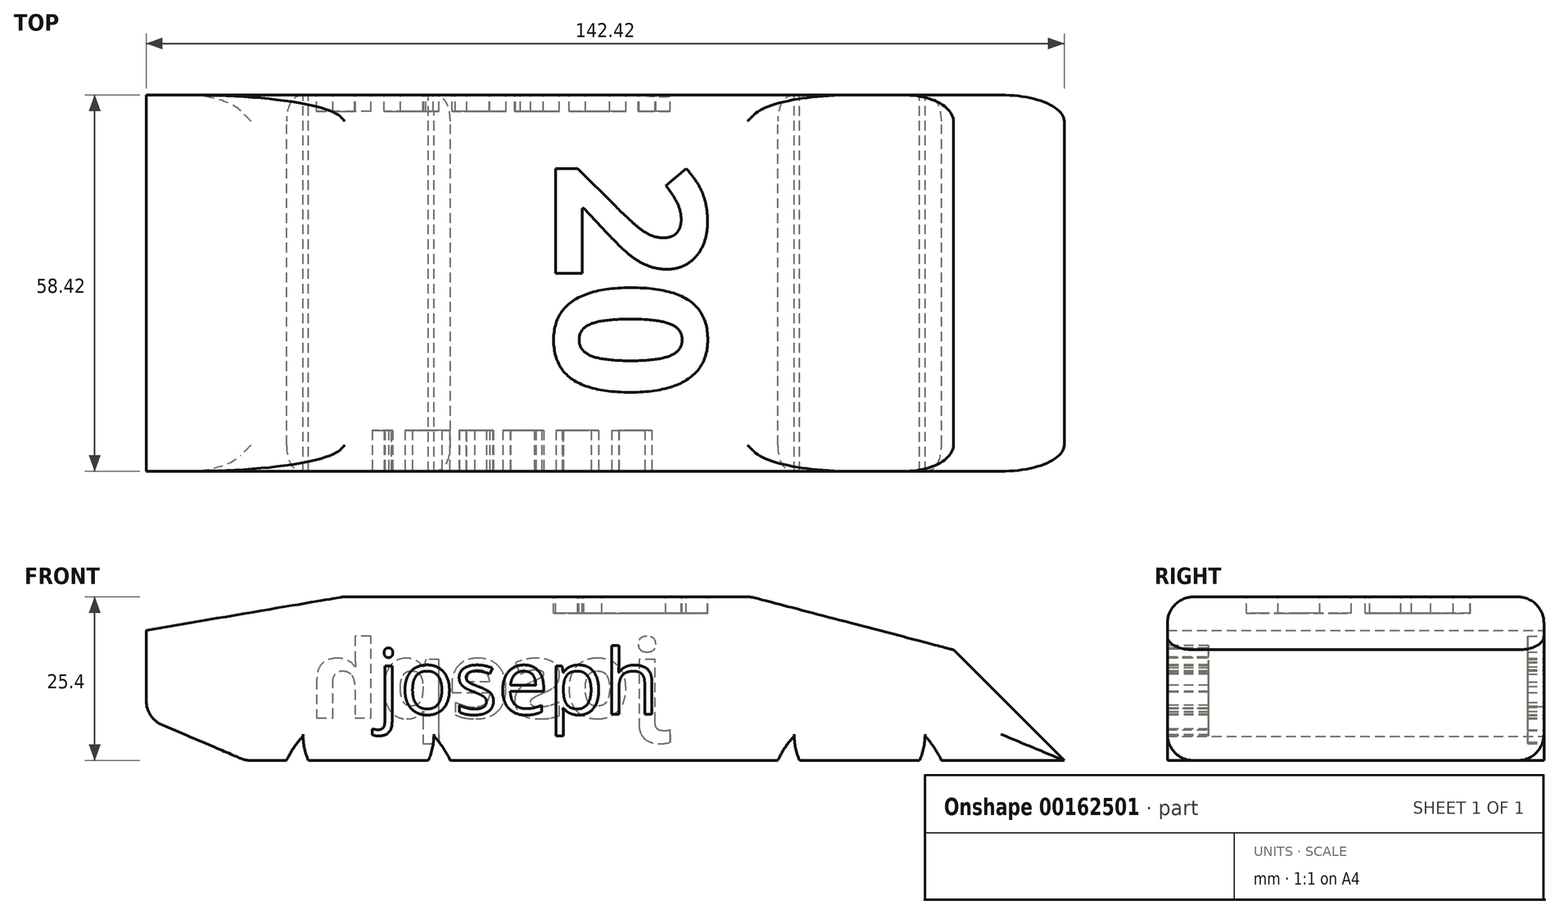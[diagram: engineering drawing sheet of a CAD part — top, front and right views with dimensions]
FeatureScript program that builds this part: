
annotation { "Feature Type Name" : "Feature", "Feature Type Description" : "" }
export const myFeature = defineFeature(function(context is Context, id is Id, definition is map)
    precondition{}
    {
        {
            var Q0;
            Q0=qCreatedBy(makeId("Front.planeOp"),FACE);
            var sketch = newSketch(context, id + "F0", { "sketchPlane" : qUnion([Q0])});
            skLineSegment(sketch, "E0", {"start": v(37.98, 0) * mm, "end": v(20.8, 17.18) * mm});
            skLineSegment(sketch, "E1", {"start": v(20.8, 17.18) * mm, "end": v(-10.62, 25.4) * mm});
            skLineSegment(sketch, "E2", {"start": v(-10.62, 25.4) * mm, "end": v(-73.96, 25.4) * mm});
            skLineSegment(sketch, "E3", {"start": v(-73.96, 25.4) * mm, "end": v(-104.44, 20.21) * mm});
            skLineSegment(sketch, "E4", {"start": v(-104.44, 20.21) * mm, "end": v(-104.44, 6.59) * mm});
            skLineSegment(sketch, "E5", {"start": v(-104.44, 6.59) * mm, "end": v(-89.02, 0) * mm});
            skLineSegment(sketch, "E6", {"start": v(-89.02, 0) * mm, "end": v(37.98, 0) * mm});
            skPoint(sketch, "E7.start.orphan", {"position": v(55.68, 0) * mm});
            skSolve(sketch);
        }
        {
            var Q0;
            Q0 = qSketchRegion(id + "F0", true);
            extrude(context, id + "F1", {"entities" : qUnion([Q0]), "endBound" : BoundingType.SYMMETRIC, "depth" : 58.42 * mm});
        }
        {
            var Q0;
            Q0=makeQuery(id+"F1.opExtrude","SWEPT_FACE",FACE,{"disambiguationData":[OSD([sQuery(id+"F0.wireOp",EDGE,"E2")])]});
            var Q1;
            Q1=makeQuery(id+"F1.opExtrude","CAP_EDGE",EDGE,{"disambiguationData":[OSD([sQuery(id+"F0.wireOp",EDGE,"E0")])],"isStart":false});
            var Q2;
            Q2=makeQuery(id+"F1.opExtrude","CAP_EDGE",EDGE,{"disambiguationData":[OSD([sQuery(id+"F0.wireOp",EDGE,"E0")])],"isStart":true});
            var Q3;
            Q3=makeQuery(id+"F1.opExtrude","CAP_EDGE",EDGE,{"disambiguationData":[OSD([sQuery(id+"F0.wireOp",EDGE,"E6")])],"isStart":false});
            var Q4;
            Q4=makeQuery(id+"F1.opExtrude","CAP_EDGE",EDGE,{"disambiguationData":[OSD([sQuery(id+"F0.wireOp",EDGE,"E6")])],"isStart":true});
            var Q5;
            Q5=makeQuery(id+"F1.opExtrude","SWEPT_EDGE",EDGE,{"disambiguationData":[OSD([sQuery(id+"F0.wireOp",EDGE,"E5"),sQuery(id+"F0.wireOp",EDGE,"E6")])]});
            var Q6;
            Q6=makeQuery(id+"F1.opExtrude","SWEPT_EDGE",EDGE,{"disambiguationData":[OSD([sQuery(id+"F0.wireOp",EDGE,"E4"),sQuery(id+"F0.wireOp",EDGE,"E5")])]});
            fillet(context, id + "F2", {"entities" : qUnion([Q0, Q1, Q2, Q3, Q4, Q5, Q6]), "radius" : 4.06 * mm, "tangentPropagation" : true, "allowEdgeOverflow" : false});
        }
        {
            var Q0;
            Q0=qCreatedBy(makeId("Front.planeOp"),FACE);
            var sketch = newSketch(context, id + "F3", { "sketchPlane" : qUnion([Q0])});
            skArc(sketch, "E8", {"start": v(18.93, 0) * mm, "mid": v(6.23, 8.15) * mm, "end": v(-6.47, 0) * mm});
            skArc(sketch, "E9", {"start": v(-57.27, 0) * mm, "mid": v(-69.97, 8.15) * mm, "end": v(-82.67, 0) * mm});
            skLineSegment(sketch, "E10", {"start": v(18.93, 0) * mm, "end": v(-6.47, 0) * mm});
            skLineSegment(sketch, "E11", {"start": v(-57.27, 0) * mm, "end": v(-82.67, 0) * mm});
            skCircle(sketch, "E12", {"center": v(-69.97, 4.06) * mm, "radius": 9.53 * mm});
            skCircle(sketch, "E13", {"center": v(6.23, 4.06) * mm, "radius": 9.53 * mm});
            skPoint(sketch, "E13.centerSnap0", {"position": v(6.23, 0) * mm});
            skSolve(sketch);
        }
        {
            var Q0;
            Q0 = qSketchRegion(id + "F3", true);
            extrude(context, id + "F4", {"entities" : qUnion([Q0]), "operationType" : NewBodyOperationType.REMOVE, "endBound" : BoundingType.SYMMETRIC, "depth" : 84.33 * mm});
        }
        {
            var Q0;
            Q0=qCreatedBy(makeId("Front.planeOp"),FACE);
            var sketch = newSketch(context, id + "F5", { "sketchPlane" : qUnion([Q0])});
            skCircle(sketch, "E14", {"center": v(6.23, 4.06) * mm, "radius": 10.16 * mm});
            skCircle(sketch, "E15", {"center": v(-69.97, 4.06) * mm, "radius": 10.16 * mm});
            skSolve(sketch);
        }
        {
            var Q0;
            Q0 = qSketchRegion(id + "F5", true);
            extrude(context, id + "F6", {"entities" : qUnion([Q0]), "operationType" : NewBodyOperationType.ADD, "endBound" : BoundingType.SYMMETRIC, "depth" : 58.42 * mm});
        }
        {
            var Q0;
            Q0=makeQuery(id+"F1.opExtrude","SWEPT_FACE",FACE,{"disambiguationData":[OSD([sQuery(id+"F0.wireOp",EDGE,"E2")])]});
            var sketch = newSketch(context, id + "F7", { "sketchPlane" : qUnion([Q0])});
            skText(sketch, "E16", { "text": "20\n\n", "fontName": "OpenSans-Bold.ttf"});
            const initialGuessF7  = {"E16": [-0.04092, 0.01905, 0, -1, 0.02343]};
            skSetInitialGuess(sketch, initialGuessF7);
            skSolve(sketch);
        }
        {
            var Q0;
            Q0 = qSketchRegion(id + "F7", true);
            extrude(context, id + "F8", {"entities" : qUnion([Q0]), "operationType" : NewBodyOperationType.REMOVE, "oppositeDirection" : true, "depth" : 2.54 * mm});
        }
        {
            var Q0;
            Q0=makeQuery(id+"F6.boolean.opBoolean","MERGE",FACE,{"derivedFrom":[makeQuery(id+"F1.opExtrude","CAP_FACE",FACE,{"disambiguationData":[OSD([sQuery(id+"F0.wireOp",EDGE,"E0"),sQuery(id+"F0.wireOp",EDGE,"E1"),sQuery(id+"F0.wireOp",EDGE,"E2"),sQuery(id+"F0.wireOp",EDGE,"E3"),sQuery(id+"F0.wireOp",EDGE,"E4"),sQuery(id+"F0.wireOp",EDGE,"E5"),sQuery(id+"F0.wireOp",EDGE,"E6")])],"isStart":true}),makeQuery(id+"F6.opExtrude","CAP_FACE",FACE,{"disambiguationData":[OSD([sQuery(id+"F5.wireOp",EDGE,"E14")])],"isStart":true}),makeQuery(id+"F6.opExtrude","CAP_FACE",FACE,{"disambiguationData":[OSD([sQuery(id+"F5.wireOp",EDGE,"E15")])],"isStart":true})]});
            var sketch = newSketch(context, id + "F9", { "sketchPlane" : qUnion([Q0])});
            skText(sketch, "E17", { "text": "joseph", "fontName": "OpenSans-Bold.ttf"});
            const initialGuessF9  = {"E17": [0.0242, 0.00662, 1, 0, 0.012]};
            skSetInitialGuess(sketch, initialGuessF9);
            skSolve(sketch);
        }
        {
            var Q0;
            Q0 = qSketchRegion(id + "F9", true);
            extrude(context, id + "F10", {"entities" : qUnion([Q0]), "operationType" : NewBodyOperationType.REMOVE, "oppositeDirection" : true, "depth" : 2.54 * mm});
        }
        {
            var Q0;
            Q0=makeQuery(id+"F6.boolean.opBoolean","MERGE",FACE,{"derivedFrom":[makeQuery(id+"F1.opExtrude","CAP_FACE",FACE,{"disambiguationData":[OSD([sQuery(id+"F0.wireOp",EDGE,"E0"),sQuery(id+"F0.wireOp",EDGE,"E1"),sQuery(id+"F0.wireOp",EDGE,"E2"),sQuery(id+"F0.wireOp",EDGE,"E3"),sQuery(id+"F0.wireOp",EDGE,"E4"),sQuery(id+"F0.wireOp",EDGE,"E5"),sQuery(id+"F0.wireOp",EDGE,"E6")])],"isStart":false}),makeQuery(id+"F6.opExtrude","CAP_FACE",FACE,{"disambiguationData":[OSD([sQuery(id+"F5.wireOp",EDGE,"E14")])],"isStart":false}),makeQuery(id+"F6.opExtrude","CAP_FACE",FACE,{"disambiguationData":[OSD([sQuery(id+"F5.wireOp",EDGE,"E15")])],"isStart":false})]});
            var sketch = newSketch(context, id + "F11", { "sketchPlane" : qUnion([Q0])});
            skText(sketch, "E18", { "text": "joseph", "fontName": "OpenSans-Regular.ttf"});
            skLineSegment(sketch, "E19", {"start": v(-46.46, 21.34) * mm, "end": v(-46.46, 17.3) * mm});
            const initialGuessF11  = {"E18": [-0.06864, 0.00719, 1, 0, 0.0101]};
            skSetInitialGuess(sketch, initialGuessF11);
            skSolve(sketch);
        }
        {
            var Q0;
            Q0 = qSketchRegion(id + "F11", true);
            extrude(context, id + "F12", {"entities" : qUnion([Q0]), "operationType" : NewBodyOperationType.REMOVE, "oppositeDirection" : true, "depth" : 6.35 * mm});
        }
        {
            var Q0;
            {var subQ0=sQuery(id+"F5.wireOp",EDGE,"E15");var subQ1=sQuery(id+"F5.wireOp",EDGE,"E14");var subQ2=sQuery(id+"F0.wireOp",EDGE,"E6");var subQ3=sQuery(id+"F0.wireOp",EDGE,"E0");var subQ4=sQuery(id+"F0.wireOp",EDGE,"E5");var subQ5=sQuery(id+"F0.wireOp",EDGE,"E3");var subQ6=sQuery(id+"F0.wireOp",EDGE,"E4");var subQ7=sQuery(id+"F0.wireOp",EDGE,"E2");var subQ8=sQuery(id+"F0.wireOp",EDGE,"E1");Q0=makeQuery(id+"F12.boolean.opBoolean","SPLIT",FACE,{"disambiguationData":[TD([makeQuery(id+"F1.opExtrude","SWEPT_FACE",FACE,{"disambiguationData":[OSD([subQ8])]})])],"derivedFrom":makeQuery(id+"F6.boolean.opBoolean","MERGE",FACE,{"derivedFrom":[makeQuery(id+"F1.opExtrude","CAP_FACE",FACE,{"disambiguationData":[OSD([subQ3,subQ8,subQ7,subQ5,subQ6,subQ4,subQ2])],"isStart":false}),makeQuery(id+"F6.opExtrude","CAP_FACE",FACE,{"disambiguationData":[OSD([subQ1])],"isStart":false}),makeQuery(id+"F6.opExtrude","CAP_FACE",FACE,{"disambiguationData":[OSD([subQ0])],"isStart":false})]})});}
            var sketch = newSketch(context, id + "F13", { "sketchPlane" : qUnion([Q0])});
            skLineSegment(sketch, "E20.bottom", {"start": v(-83.28, 0) * mm, "end": v(26.75, 0) * mm});
            skLineSegment(sketch, "E20.top", {"start": v(-83.28, -13.54) * mm, "end": v(26.75, -13.54) * mm});
            skLineSegment(sketch, "E20.left", {"start": v(-83.28, 0) * mm, "end": v(-83.28, -13.54) * mm});
            skLineSegment(sketch, "E20.right", {"start": v(26.75, 0) * mm, "end": v(26.75, -13.54) * mm});
            skSolve(sketch);
        }
        {
            var Q0;
            Q0 = qSketchRegion(id + "F13", true);
            extrude(context, id + "F14", {"entities" : qUnion([Q0]), "operationType" : NewBodyOperationType.REMOVE, "oppositeDirection" : true, "depth" : 76.2 * mm});
        }
    });
